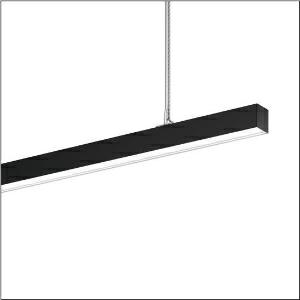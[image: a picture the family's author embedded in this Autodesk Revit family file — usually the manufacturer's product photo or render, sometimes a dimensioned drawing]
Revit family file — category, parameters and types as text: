
# Revit family: silica_r__21_51mx30db45bb_77a6
name_source: partatom
category: Lighting Fixtures
units: mm (PartAtom-declared; Revit-internal decimal feet)

## family parameters
Cut with Voids When Loaded = No
Host = Face
Light Source = No
Part Type = Normal
Room Calculation Point = No
Round Connector Dimension = Use Diameter
Shared = No

## types (1)
- --- (1 x LED, 5260 lm, 32 W, 4000K)
    Apparent Load = 32 VA
    CIE Flux Codes = 47 79 96 57 100
    Color Rendering = 80
    Color Temperature = 4000K
    Default Elevation = 1800 mm
    Description = Silica® 21, office luminaire, primary optical cover: cover, of PMMA, opal, light emission: direct/indirect distribution, primary light characteristic: symmetric, installation type: suspended mounting, LED, rated luminous flux: 5.260lm, luminous efficacy: 164lm/W, light colour: 840, colour temperature: 4000K, with terminal, 3+2-pole, max. 2.5mm², mains connection: 220..240V, AC, 50/60Hz, rated input power: 32W, luminaire housing, of aluminium, jet black (RAL 9005), length: 1.504mm, width: 53mm, height: 53mm, protection rating (complete): IP20, insulation class (complete): insulation class I (protective earthing), certification: CE, permissible operating ambient temperature: 0..+35°C, standard: EN 50419, packaging unit: 1 piece
    Height = 53 mm
    Lamp = 1 x LED
    Lamp Light Flux = 5260 lm
    Lamp Power = 32 W
    Lamp count = 1
    Length = 1504 mm
    Luminous efficacy = 164 lm/W
    Manufacturer = Siteco
    ModVariant = No
    Model = 51MX30DB45BB
    Mounting Place = Ceiling
    Mounting Type = Pendant
    Number of Poles = 1
    OnlyDefault = Yes
    Power Factor = 1
    Product Name = Silica® 21
    Product group = office luminaire | ceiling pendant
    ProductGroupID = 902
    Protection Class = Protection class I
    Protection Degree = IP 20
    RLX_Detail_Level = 1
    RLX_Emergency_Light_Flux = 0 lm
    RLX_Emergency_Type = 0
    RLX_Emergency_Type_DB = No
    RlxData = <blob elided: 25921 chars, md5=c9fff697>
    Socket = socket
    Standby Power = 0 W
    System Light Flux = 5260 lm
    System Power = 32 W
    Type Comments = factory setting: luminous flux: 100 % | dim-lin: 254 | 218 mA
    Type Image = l_1297744.jpg
    URL = http://relux.com
    VarID = @adj_047059
    Voltage = 0 V
    Weight = 0.00 kg
    Width = 53 mm

## geometry (parser evidence)
native form markers: Blend x4, Sweep x11
no freeform markers — native parametric forms only
